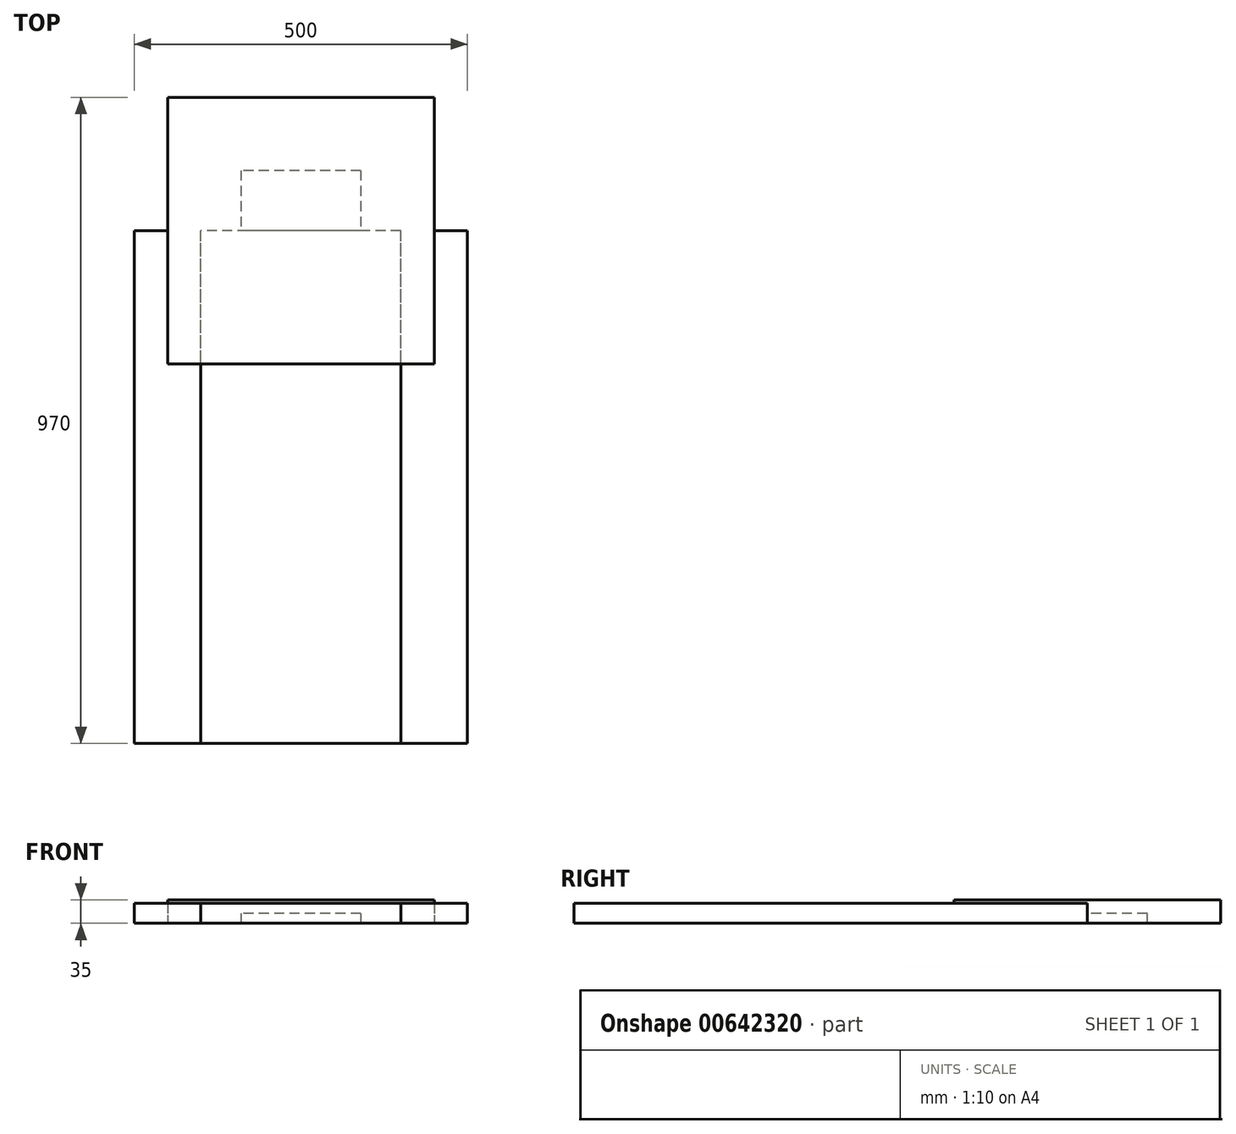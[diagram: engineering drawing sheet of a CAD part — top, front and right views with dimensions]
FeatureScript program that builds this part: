
annotation { "Feature Type Name" : "Feature", "Feature Type Description" : "" }
export const myFeature = defineFeature(function(context is Context, id is Id, definition is map)
    precondition{}
    {
        {
            var Q0;
            Q0=qCreatedBy(makeId("Front.planeOp"),FACE);
            var sketch = newSketch(context, id + "F0", { "sketchPlane" : qUnion([Q0])});
            skLineSegment(sketch, "E0.bottom", {"start": v(250, -15) * mm, "end": v(-250, -15) * mm});
            skLineSegment(sketch, "E0.top", {"start": v(250, 15) * mm, "end": v(-250, 15) * mm});
            skLineSegment(sketch, "E0.left", {"start": v(250, -15) * mm, "end": v(250, 15) * mm});
            skLineSegment(sketch, "E0.right", {"start": v(-250, -15) * mm, "end": v(-250, 15) * mm});
            skPoint(sketch, "E0.middle", {"position": v(0, 0) * mm});
            skSolve(sketch);
        }
        {
            var Q0;
            Q0=makeQuery(id+"F0.imprint","IMPRINT",FACE,{"disambiguationData":[TD([[makeQuery(id+"F0.imprint","IMPRINT",EDGE,{"derivedFrom":sQuery(id+"F0.wireOp",EDGE,"E0.bottom")}),-1.0]])]});
            extrude(context, id + "F1", {"entities" : qUnion([Q0]), "depth" : 770 * mm, "offsetDistance" : 25 * mm});
        }
        {
            var Q0;
            Q0=qCreatedBy(makeId("Top.planeOp"),FACE);
            var sketch = newSketch(context, id + "F2", { "sketchPlane" : qUnion([Q0])});
            skLineSegment(sketch, "E1.bottom", {"start": v(200, -200) * mm, "end": v(-200, -200) * mm});
            skLineSegment(sketch, "E1.top", {"start": v(200, 200) * mm, "end": v(-200, 200) * mm});
            skLineSegment(sketch, "E1.left", {"start": v(200, -200) * mm, "end": v(200, 200) * mm});
            skLineSegment(sketch, "E1.right", {"start": v(-200, -200) * mm, "end": v(-200, 200) * mm});
            skPoint(sketch, "E1.middle", {"position": v(0, 0) * mm});
            skSolve(sketch);
        }
        {
            var Q0;
            Q0=makeQuery(id+"F2.imprint","IMPRINT",FACE,{"disambiguationData":[TD([[makeQuery(id+"F2.imprint","IMPRINT",EDGE,{"derivedFrom":sQuery(id+"F2.wireOp",EDGE,"E1.bottom")}),-1.0]])]});
            extrude(context, id + "F3", {"entities" : qUnion([Q0]), "depth" : 20 * mm, "offsetDistance" : 25 * mm});
        }
        {
            var Q0;
            Q0=makeQuery(id+"F3.opExtrude","CAP_FACE",FACE,{"disambiguationData":[OSD([sQuery(id+"F2.wireOp",EDGE,"E1.bottom"),sQuery(id+"F2.wireOp",EDGE,"E1.top"),sQuery(id+"F2.wireOp",EDGE,"E1.left"),sQuery(id+"F2.wireOp",EDGE,"E1.right")])],"isStart":true});
            var sketch = newSketch(context, id + "F4", { "sketchPlane" : qUnion([Q0])});
            skLineSegment(sketch, "E2.bottom", {"start": v(90, -90) * mm, "end": v(-90, -90) * mm});
            skLineSegment(sketch, "E2.top", {"start": v(90, 90) * mm, "end": v(-90, 90) * mm});
            skLineSegment(sketch, "E2.left", {"start": v(90, -90) * mm, "end": v(90, 90) * mm});
            skLineSegment(sketch, "E2.right", {"start": v(-90, -90) * mm, "end": v(-90, 90) * mm});
            skPoint(sketch, "E2.middle", {"position": v(0, 0) * mm});
            skSolve(sketch);
        }
        {
            var Q0;
            Q0=makeQuery(id+"F4.imprint","IMPRINT",FACE,{"disambiguationData":[TD([[makeQuery(id+"F4.imprint","IMPRINT",EDGE,{"derivedFrom":sQuery(id+"F4.wireOp",EDGE,"E2.bottom")}),1.0]])]});
            extrude(context, id + "F5", {"entities" : qUnion([Q0]), "operationType" : NewBodyOperationType.ADD, "depth" : 15 * mm, "offsetDistance" : 25 * mm});
        }
        {
            var Q0;
            Q0=qCreatedBy(makeId("Front.planeOp"),FACE);
            var sketch = newSketch(context, id + "F6", { "sketchPlane" : qUnion([Q0])});
            skLineSegment(sketch, "E3.bottom", {"start": v(150, -15) * mm, "end": v(-150, -15) * mm});
            skLineSegment(sketch, "E3.top", {"start": v(150, 15) * mm, "end": v(-150, 15) * mm});
            skLineSegment(sketch, "E3.left", {"start": v(150, -15) * mm, "end": v(150, 15) * mm});
            skLineSegment(sketch, "E3.right", {"start": v(-150, -15) * mm, "end": v(-150, 15) * mm});
            skPoint(sketch, "E3.middle", {"position": v(0, 0) * mm});
            skSolve(sketch);
        }
        {
            var Q0;
            Q0=makeQuery(id+"F6.imprint","IMPRINT",FACE,{"disambiguationData":[TD([[makeQuery(id+"F6.imprint","IMPRINT",EDGE,{"derivedFrom":sQuery(id+"F6.wireOp",EDGE,"E3.bottom")}),-1.0]])]});
            extrude(context, id + "F7", {"entities" : qUnion([Q0]), "depth" : 770 * mm, "offsetDistance" : 25 * mm});
        }
    });
